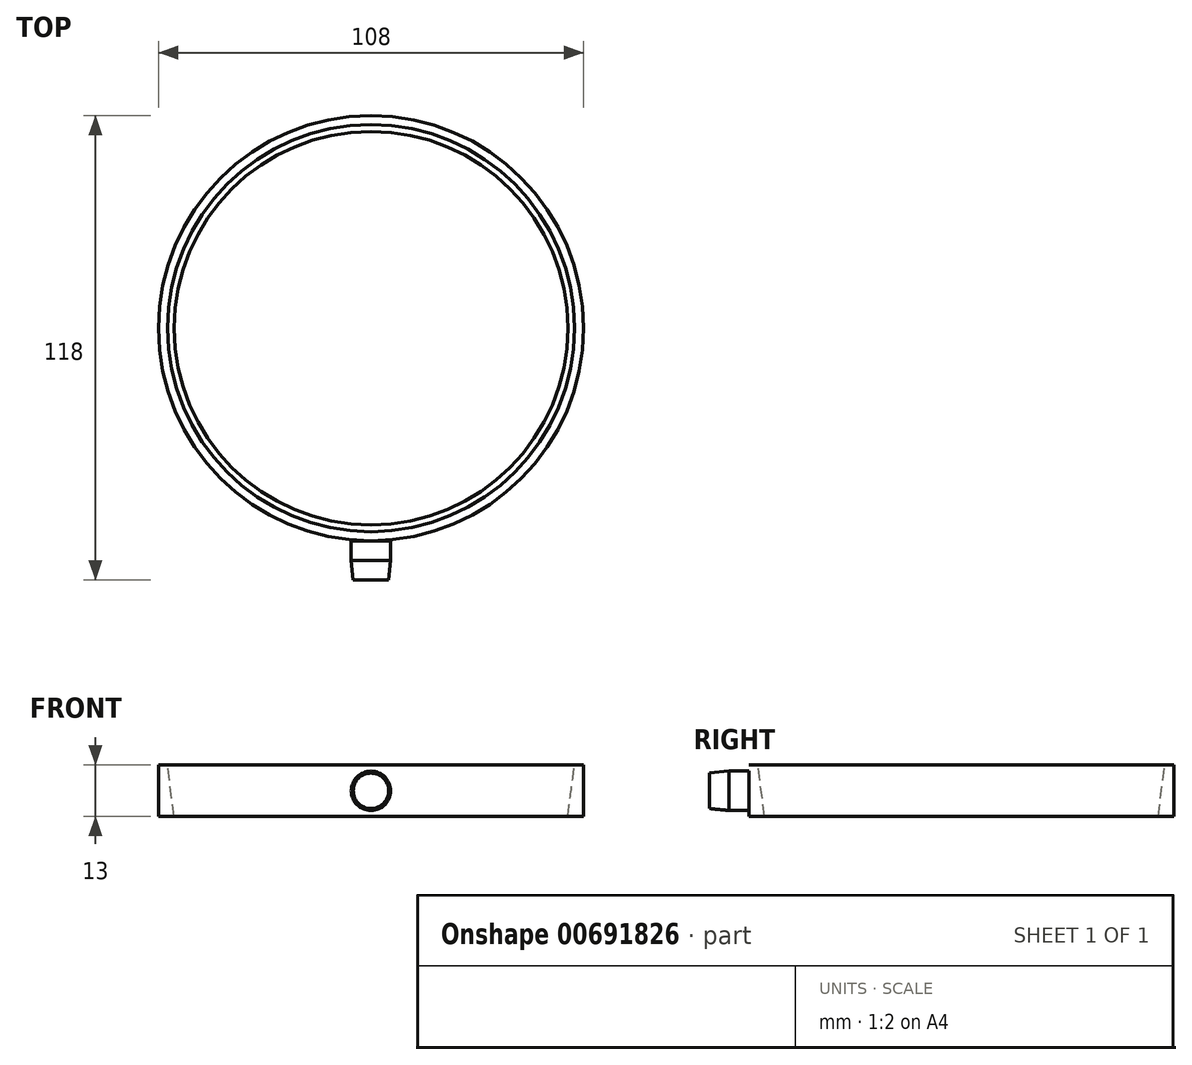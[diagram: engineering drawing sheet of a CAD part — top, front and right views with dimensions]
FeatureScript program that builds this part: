
annotation { "Feature Type Name" : "Feature", "Feature Type Description" : "" }
export const myFeature = defineFeature(function(context is Context, id is Id, definition is map)
    precondition{}
    {
        {
            var Q0;
            Q0=qCreatedBy(makeId("Top.planeOp"),FACE);
            var sketch = newSketch(context, id + "F0", { "sketchPlane" : qUnion([Q0])});
            skCircle(sketch, "E0", {"center": v(0, 0) * mm, "radius": 50 * mm});
            skCircle(sketch, "E1.0", {"center": v(0, 0) * mm, "radius": 54 * mm});
            skSolve(sketch);
        }
        {
            var Q0;
            Q0=makeQuery(id+"F0.imprint","IMPRINT",FACE,{"disambiguationData":[TD([[makeQuery(id+"F0.imprint","IMPRINT",EDGE,{"derivedFrom":sQuery(id+"F0.wireOp",EDGE,"E0")}),-1.0]])]});
            extrude(context, id + "F1", {"entities" : qUnion([Q0]), "depth" : 13 * mm, "offsetDistance" : 25 * mm});
        }
        {
            var Q0;
            Q0=qCreatedBy(makeId("Front.planeOp"),FACE);
            cPlane(context, id + "F2", {"entities" : qUnion([Q0]), "cplaneType" : CPlaneType.OFFSET, "offset" : 54 * mm, "width" : 150 * mm, "height" : 150 * mm});
        }
        {
            var Q0;
            Q0=qCreatedBy(id+"F2.planeOp",FACE);
            var sketch = newSketch(context, id + "F3", { "sketchPlane" : qUnion([Q0])});
            skCircle(sketch, "E2", {"center": v(0, 6.46) * mm, "radius": 5 * mm});
            skSolve(sketch);
        }
        {
            var Q0;
            Q0=qSketchRegion(id+"F3",true);
            var Q1;
            Q1=sQuery(id+"F3.wireOp",EDGE,"E2");
            extrude(context, id + "F4", {"entities" : qUnion([Q0]), "operationType" : NewBodyOperationType.ADD, "surfaceEntities" : qUnion([Q1]), "depth" : 10 * mm, "offsetDistance" : 25 * mm});
        }
        {
            var Q0;
            Q0=makeQuery(id+"F1.opExtrude","CAP_EDGE",EDGE,{"disambiguationData":[OSD([sQuery(id+"F0.wireOp",EDGE,"E0")])],"isStart":false});
            chamfer(context, id + "F5", {"entities" : qUnion([Q0]), "chamferType" : ChamferType.OFFSET_ANGLE, "width" : 13 * mm, "oppositeDirection" : false, "angle" : 7.5 * degree, "tangentPropagation" : true});
        }
        {
            var Q0;
            Q0=makeQuery(id+"F4.opExtrude","CAP_EDGE",EDGE,{"disambiguationData":[OSD([sQuery(id+"F3.wireOp",EDGE,"E2")])],"isStart":false});
            chamfer(context, id + "F6", {"entities" : qUnion([Q0]), "chamferType" : ChamferType.TWO_OFFSETS, "width1" : .5 * mm, "oppositeDirection" : false, "width2" : 5 * mm, "tangentPropagation" : true});
        }
    });
